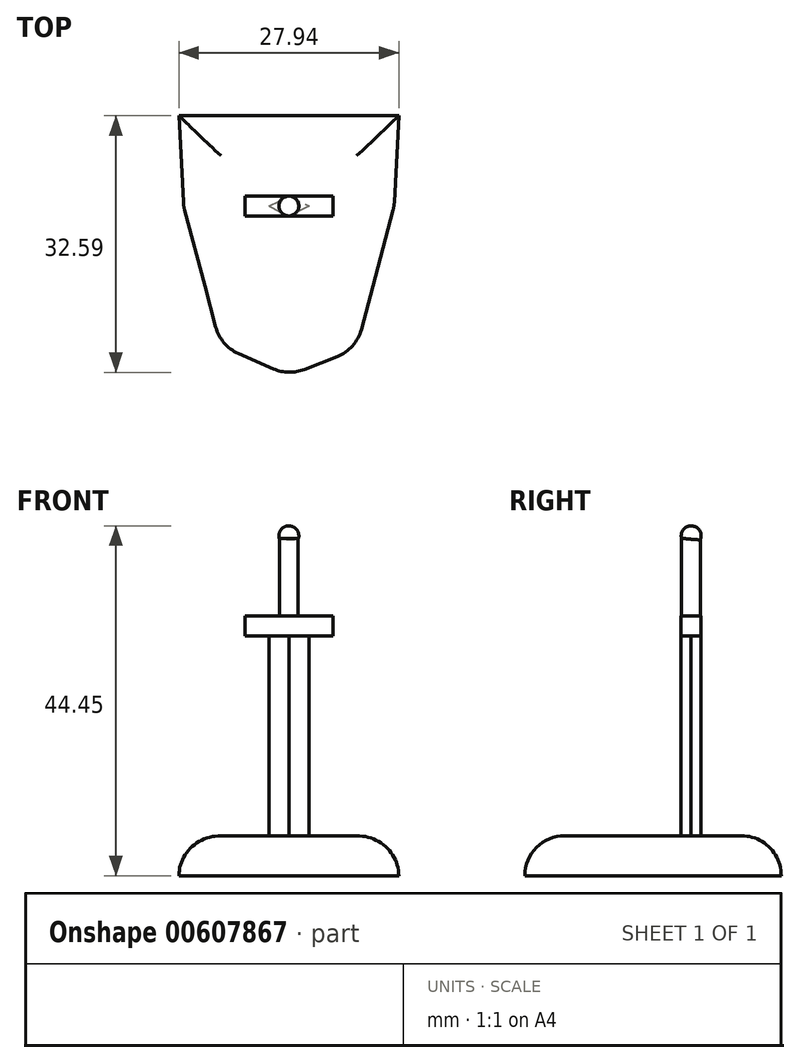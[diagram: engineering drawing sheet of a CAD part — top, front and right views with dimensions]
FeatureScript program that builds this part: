
annotation { "Feature Type Name" : "Feature", "Feature Type Description" : "" }
export const myFeature = defineFeature(function(context is Context, id is Id, definition is map)
    precondition{}
    {
        {
            var Q0;
            Q0=qCreatedBy(makeId("Top.planeOp"),FACE);
            var sketch = newSketch(context, id + "F0", { "sketchPlane" : qUnion([Q0])});
            skLineSegment(sketch, "E0", {"start": v(0, 11.49) * mm, "end": v(-13.97, 11.49) * mm});
            skLineSegment(sketch, "E1", {"start": v(-13.97, 11.49) * mm, "end": v(-13.37, 0) * mm});
            skLineSegment(sketch, "E2", {"start": v(-13.37, 0) * mm, "end": v(13.37, 0) * mm});
            skLineSegment(sketch, "E3", {"start": v(13.37, 0) * mm, "end": v(13.97, 11.49) * mm});
            skLineSegment(sketch, "E4", {"start": v(13.97, 11.49) * mm, "end": v(0, 11.49) * mm});
            skLineSegment(sketch, "E5", {"start": v(-13.42, 0.16) * mm, "end": v(-13.37, 0) * mm});
            skArc(sketch, "E6.trimOffspring", {"start": v(-13.37, 0) * mm, "mid": v(-13.4, 0.1) * mm, "end": v(-13.43, 0.21) * mm});
            skLineSegment(sketch, "E7", {"start": v(-13.37, 0) * mm, "end": v(-10.67, -10.16) * mm});
            skLineSegment(sketch, "E8", {"start": v(-10.67, -10.16) * mm, "end": v(-8.66, -17.71) * mm});
            skLineSegment(sketch, "E9", {"start": v(10.67, -10.16) * mm, "end": v(8.54, -18.14) * mm});
            skLineSegment(sketch, "E10", {"start": v(13.37, 0) * mm, "end": v(10.67, -10.16) * mm});
            skLineSegment(sketch, "E11", {"start": v(-8.66, -17.71) * mm, "end": v(0, -21.52) * mm});
            skLineSegment(sketch, "E12", {"start": v(0, -21.52) * mm, "end": v(8.54, -18.14) * mm});
            skPoint(sketch, "E13.orphan", {"position": v(0, -50.2) * mm});
            skSolve(sketch);
        }
        {
            var Q0;
            Q0 = qSketchRegion(id + "F0", true);
            extrude(context, id + "F1", {"entities" : qUnion([Q0]), "depth" : 5.08 * mm, "offsetDistance" : 25.4 * mm});
        }
        {
            var Q0;
            Q0=makeQuery(id+"F1.opExtrude","CAP_FACE",FACE,{"disambiguationData":[OSD([sQuery(id+"F0.wireOp",EDGE,"E0"),sQuery(id+"F0.wireOp",EDGE,"E1"),sQuery(id+"F0.wireOp",EDGE,"E3"),sQuery(id+"F0.wireOp",EDGE,"E4"),sQuery(id+"F0.wireOp",EDGE,"E7"),sQuery(id+"F0.wireOp",EDGE,"E8"),sQuery(id+"F0.wireOp",EDGE,"E9"),sQuery(id+"F0.wireOp",EDGE,"E10"),sQuery(id+"F0.wireOp",EDGE,"E11"),sQuery(id+"F0.wireOp",EDGE,"E12")])],"isStart":false});
            var sketch = newSketch(context, id + "F2", { "sketchPlane" : qUnion([Q0])});
            skLineSegment(sketch, "E14", {"start": v(0, 1.27) * mm, "end": v(2.54, 0) * mm});
            skLineSegment(sketch, "E15", {"start": v(2.54, 0) * mm, "end": v(0, -1.27) * mm});
            skLineSegment(sketch, "E16", {"start": v(-2.54, 0) * mm, "end": v(0, -1.27) * mm});
            skLineSegment(sketch, "E17", {"start": v(-2.54, 0) * mm, "end": v(0, 1.27) * mm});
            skPoint(sketch, "E18.start.orphan", {"position": v(0, 0) * mm});
            skSolve(sketch);
        }
        {
            var Q0;
            Q0 = qSketchRegion(id + "F2", true);
            extrude(context, id + "F3", {"entities" : qUnion([Q0]), "operationType" : NewBodyOperationType.ADD, "depth" : 25.4 * mm, "offsetDistance" : 25.4 * mm});
        }
        {
            var Q0;
            Q0=makeQuery(id+"F3.opExtrude","CAP_FACE",FACE,{"disambiguationData":[OSD([sQuery(id+"F2.wireOp",EDGE,"E14"),sQuery(id+"F2.wireOp",EDGE,"E15"),sQuery(id+"F2.wireOp",EDGE,"E16"),sQuery(id+"F2.wireOp",EDGE,"E17")])],"isStart":false});
            var sketch = newSketch(context, id + "F4", { "sketchPlane" : qUnion([Q0])});
            skLineSegment(sketch, "E19", {"start": v(0, 1.27) * mm, "end": v(-5.59, 1.27) * mm});
            skLineSegment(sketch, "E20", {"start": v(-5.59, 1.27) * mm, "end": v(-5.59, -1.27) * mm});
            skLineSegment(sketch, "E21", {"start": v(-5.59, -1.27) * mm, "end": v(0, -1.27) * mm});
            skLineSegment(sketch, "E22", {"start": v(0, 1.27) * mm, "end": v(5.59, 1.27) * mm});
            skLineSegment(sketch, "E23", {"start": v(5.59, 1.27) * mm, "end": v(5.59, -1.27) * mm});
            skLineSegment(sketch, "E24", {"start": v(5.59, -1.27) * mm, "end": v(0, -1.27) * mm});
            skSolve(sketch);
        }
        {
            var Q0;
            Q0 = qSketchRegion(id + "F4", true);
            extrude(context, id + "F5", {"entities" : qUnion([Q0]), "operationType" : NewBodyOperationType.ADD, "depth" : 2.54 * mm, "offsetDistance" : 25.4 * mm});
        }
        {
            var Q0;
            Q0=makeQuery(id+"F5.opExtrude","CAP_FACE",FACE,{"disambiguationData":[OSD([sQuery(id+"F4.wireOp",EDGE,"E19"),sQuery(id+"F4.wireOp",EDGE,"E20"),sQuery(id+"F4.wireOp",EDGE,"E21"),sQuery(id+"F4.wireOp",EDGE,"E22"),sQuery(id+"F4.wireOp",EDGE,"E23"),sQuery(id+"F4.wireOp",EDGE,"E24")])],"isStart":false});
            var sketch = newSketch(context, id + "F6", { "sketchPlane" : qUnion([Q0])});
            skCircle(sketch, "E25", {"center": v(0, 0) * mm, "radius": 1.2 * mm});
            skSolve(sketch);
        }
        {
            var Q0;
            Q0 = qSketchRegion(id + "F6", true);
            extrude(context, id + "F7", {"entities" : qUnion([Q0]), "operationType" : NewBodyOperationType.ADD, "depth" : 10.16 * mm, "offsetDistance" : 25.4 * mm});
        }
        {
            var Q0;
            Q0=makeQuery(id+"F7.opExtrude","CAP_FACE",FACE,{"disambiguationData":[OSD([sQuery(id+"F6.wireOp",EDGE,"E25")])],"isStart":false});
            var sketch = newSketch(context, id + "F8", { "sketchPlane" : qUnion([Q0])});
            skSolve(sketch);
        }
        {
            var Q0;
            Q0=makeQuery(id+"F8.imprint","IMPRINT",FACE,{"disambiguationData":[TD([[makeQuery(id+"F8.imprint","IMPRINT",EDGE,{"derivedFrom":makeQuery(id+"F7.opExtrude","CAP_EDGE",EDGE,{"disambiguationData":[OSD([sQuery(id+"F6.wireOp",EDGE,"E25")])],"isStart":false})}),1.0]])]});
            var sketch = newSketch(context, id + "F9", { "sketchPlane" : qUnion([Q0])});
            skLineSegment(sketch, "E26", {"start": v(0, 1.3) * mm, "end": v(0, -1.23) * mm});
            skArc(sketch, "E27", {"start": v(0, -1.23) * mm, "mid": v(1.27, 0.04) * mm, "end": v(0, 1.3) * mm});
            skSolve(sketch);
        }
        {
            var Q0;
            Q0 = qSketchRegion(id + "F9", true);
            var Q1;
            Q1=sQuery(id+"F9.wireOp",EDGE,"E26");
            revolve(context, id + "F10", {"operationType" : NewBodyOperationType.ADD, "entities" : qUnion([Q0]), "axis" : qUnion([Q1]), "revolveType" : RevolveType.FULL});
        }
        {
            var Q0;
            Q0=makeQuery(id+"F1.opExtrude","CAP_EDGE",EDGE,{"disambiguationData":[OSD([sQuery(id+"F0.wireOp",EDGE,"E0"),sQuery(id+"F0.wireOp",EDGE,"E4")])],"isStart":false});
            var Q1;
            Q1=makeQuery(id+"F1.opExtrude","CAP_EDGE",EDGE,{"disambiguationData":[OSD([sQuery(id+"F0.wireOp",EDGE,"E1")])],"isStart":false});
            var Q2;
            Q2=makeQuery(id+"F1.opExtrude","CAP_EDGE",EDGE,{"disambiguationData":[OSD([sQuery(id+"F0.wireOp",EDGE,"E7")])],"isStart":false});
            var Q3;
            Q3=makeQuery(id+"F1.opExtrude","CAP_EDGE",EDGE,{"disambiguationData":[OSD([sQuery(id+"F0.wireOp",EDGE,"E11")])],"isStart":false});
            var Q4;
            Q4=makeQuery(id+"F1.opExtrude","CAP_EDGE",EDGE,{"disambiguationData":[OSD([sQuery(id+"F0.wireOp",EDGE,"E12")])],"isStart":false});
            var Q5;
            Q5=makeQuery(id+"F1.opExtrude","CAP_EDGE",EDGE,{"disambiguationData":[OSD([sQuery(id+"F0.wireOp",EDGE,"E9")])],"isStart":false});
            var Q6;
            Q6=makeQuery(id+"F1.opExtrude","CAP_EDGE",EDGE,{"disambiguationData":[OSD([sQuery(id+"F0.wireOp",EDGE,"E10")])],"isStart":false});
            var Q7;
            Q7=makeQuery(id+"F1.opExtrude","CAP_EDGE",EDGE,{"disambiguationData":[OSD([sQuery(id+"F0.wireOp",EDGE,"E3")])],"isStart":false});
            var Q8;
            Q8=makeQuery(id+"F1.opExtrude","CAP_EDGE",EDGE,{"disambiguationData":[OSD([sQuery(id+"F0.wireOp",EDGE,"E8")])],"isStart":false});
            fillet(context, id + "F11", {"entities" : qUnion([Q0, Q1, Q2, Q3, Q4, Q5, Q6, Q7, Q8]), "radius" : 5.08 * mm, "tangentPropagation" : true, "allowEdgeOverflow" : false});
        }
        {
            var Q0;
            Q0=makeQuery(id+"F11.opFillet","BLEND_EDGE",EDGE,{"blendedFrom":[makeQuery(id+"F1.opExtrude","CAP_EDGE",EDGE,{"disambiguationData":[OSD([sQuery(id+"F0.wireOp",EDGE,"E8")])],"isStart":false}),makeQuery(id+"F1.opExtrude","CAP_EDGE",EDGE,{"disambiguationData":[OSD([sQuery(id+"F0.wireOp",EDGE,"E11")])],"isStart":false})],"blendedInto":[]});
            var Q1;
            Q1=makeQuery(id+"F11.opFillet","BLEND_EDGE",EDGE,{"blendedFrom":[makeQuery(id+"F1.opExtrude","CAP_EDGE",EDGE,{"disambiguationData":[OSD([sQuery(id+"F0.wireOp",EDGE,"E11")])],"isStart":false}),makeQuery(id+"F1.opExtrude","CAP_EDGE",EDGE,{"disambiguationData":[OSD([sQuery(id+"F0.wireOp",EDGE,"E12")])],"isStart":false})],"blendedInto":[]});
            var Q2;
            Q2=makeQuery(id+"F11.opFillet","BLEND_EDGE",EDGE,{"blendedFrom":[makeQuery(id+"F1.opExtrude","CAP_EDGE",EDGE,{"disambiguationData":[OSD([sQuery(id+"F0.wireOp",EDGE,"E9")])],"isStart":false}),makeQuery(id+"F1.opExtrude","CAP_EDGE",EDGE,{"disambiguationData":[OSD([sQuery(id+"F0.wireOp",EDGE,"E12")])],"isStart":false})],"blendedInto":[]});
            var Q3;
            Q3=makeQuery(id+"F11.opFillet","BLEND_EDGE",EDGE,{"blendedFrom":[makeQuery(id+"F1.opExtrude","CAP_EDGE",EDGE,{"disambiguationData":[OSD([sQuery(id+"F0.wireOp",EDGE,"E3")])],"isStart":false}),makeQuery(id+"F1.opExtrude","CAP_EDGE",EDGE,{"disambiguationData":[OSD([sQuery(id+"F0.wireOp",EDGE,"E10")])],"isStart":false})],"blendedInto":[]});
            var Q4;
            Q4=makeQuery(id+"F11.opFillet","BLEND_EDGE",EDGE,{"blendedFrom":[makeQuery(id+"F1.opExtrude","CAP_EDGE",EDGE,{"disambiguationData":[OSD([sQuery(id+"F0.wireOp",EDGE,"E1")])],"isStart":false}),makeQuery(id+"F1.opExtrude","CAP_EDGE",EDGE,{"disambiguationData":[OSD([sQuery(id+"F0.wireOp",EDGE,"E7")])],"isStart":false})],"blendedInto":[]});
            fillet(context, id + "F12", {"entities" : qUnion([Q0, Q1, Q2, Q3, Q4]), "radius" : 5.08 * mm, "tangentPropagation" : true, "allowEdgeOverflow" : false});
        }
    });
